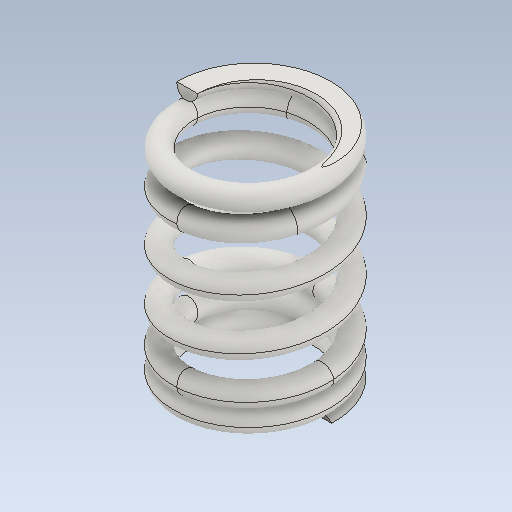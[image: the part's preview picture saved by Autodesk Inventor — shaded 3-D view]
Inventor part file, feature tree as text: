
AUTODESK INVENTOR PART (.ipt)
format: ipt  version: 2021 (Build 250183000, 183)  size: 877,568 bytes
history: native  units: in
note: dims shown in document units (in); Inventor stores cm internally (conversion verified against a paired STEP export)
features: other x73, extrude x8, sweep x2, helix x2, plane x1
ambient origin geometry x8: Origin, YZ Plane, XZ Plane, XY Plane, X Axis, Y Axis, Z Axis, Center Point
bodies: Solid1 (feature_tree)
feature tree (86):
  other  "Main Coil Path(Right)"
  other  "Section Work Plane(Right)"
  other  "Start Work Plane(Right)"
  other  "End Work Plane(Right)"
  other  "End Cut Work Plane(Right)"
  other  "Start Cut Work Plane(Right)"
  other  "Plain Ends Cut Work Plane 1(Right)"
  other  "Plain Ends Cut Work Plane 2(Right)"
  sweep  "Main Coil Feature(R)"
  other  "Start Transition Coil 1(Right)"
  other  "Start Transition Coil 2(Right)"
  other  "Start Transition Coil 3(Right)"
  other  "Start Transition Coil 4(Right)"
  other  "Start Ends Coil(Right)"
  extrude  "Start Cut Feature(Right)"  Depth=0.4866in
  other  "End Transition Coil 1(Right)"
  other  "End Transition Coil 2(Right)"
  other  "End Transition Coil 3(Right)"
  other  "End Transition Coil 4(Right)"
  other  "End Coil(Right)"
  extrude  "End Cut Feature(Right)"  Depth=0.4306in
  extrude  "Plain Ends Cut Feature 1(Right)"  Depth=0.2in
  extrude  "Plain Ends Cut Feature 2(Right)"  TaperAngle=0.0deg  [1 undecoded]
  other  "Main Coil Path(Left)"
  other  "Section Work Plane(Left)"
  other  "Start Work Plane(Left)"
  other  "End Work Plane(Left)"
  other  "End Cut Work Plane(Left)"
  other  "Start Cut Work Plane(Left)"
  other  "Plain Ends Cut Work Plane 1(Left)"
  other  "Plain Ends Cut Work Plane 2(Left)"
  sweep  "Main Coil Feature(L)"
  other  "Start Transition Coil 1(Left)"
  other  "Start Transition Coil 2(Left)"
  other  "Start Transition Coil 3(Left)"
  other  "Start Transition Coil 4(Left)"
  other  "Start Ends Coil(Left)"
  extrude  "Start Cut Feature(Left)"  Depth=0.2014in
  other  "End Transition Coil 1(Left)"
  other  "End Transition Coil 2(Left)"
  other  "End Transition Coil 3(Left)"
  other  "End Transition Coil 4(Left)"
  other  "End Coil(Left)"
  extrude  "End Cut Feature(Left)"  Depth=0.3937in
  extrude  "Cut Plain Ends Cut 1(L)"  Depth=1.5in
  extrude  "Cut Plain Ends Cut 2(L)"  Depth=0.2in
  other  "iMate Based Work Plane"
  other  "Preview Center Point"
  other  "Preview X Axis"
  other  "Path Section Sketch(Right)"
  other  "Srf1"
  helix  "Coil Section Sketch(Right)"  [1 undecoded]
  other  "Start Transition Coil Sketch 1(Right)"
  other  "Start Transition Coil Sketch 2(Right)"
  other  "Start Transition Coil Sketch 3(Right)"
  other  "Start Transition Coil Sketch 4(Right)"
  other  "End Transition Coil Sketch 1(Right)"
  other  "End Transition Coil Sketch 2(Right)"
  other  "End Transition Coil Sketch 3(Right)"
  other  "End Transition Coil Sketch 4(Right)"
  other  "Start Ends Skecth(Right)"
  other  "End Coil Skecth(Right)"
  other  "Start Cut Sketch(Right)"
  other  "End Cut Sketch(Right)"
  other  "Plain Ends Cut Sketch 2(Right)"
  other  "Plain Ends Cut Sketch 1(Right)"
  other  "Path Section Sketch(Left)"
  other  "Srf2"
  helix  "Coil Section Sketch(Left)"  [1 undecoded]
  other  "Start Transition Coil Sketch 1(Left)"
  other  "Start Transition Coil Sketch 2(Left)"
  other  "Start Transition Coil Sketch 3(Left)"
  other  "Start Transition Coil Sketch 4(Left)"
  other  "Start Ends Skecth(Left)"
  other  "Start Cut Sketch(Left)"
  other  "End Transition Coil Sketch 1(Left)"
  other  "End Transition Coil Sketch 2(Left)"
  other  "End Transition Coil Sketch 3(Left)"
  other  "End Transition Coil Sketch 4(Left)"
  other  "End Coil Skecth(Left)"
  other  "End Cut Sketch(Left)"
  other  "Plain Ends Cut Sketch 2(Left)"
  other  "Plain Ends Cut Sketch 1(Left)"
  plane  "Work Plane Start Section"
  other  "Basic Curve(Right)"
  other  "Basic Curve(Left)"
note: 3 required parameter values undecoded (feature->parameter linkage not recoverable at this tier; creation-order binding heuristic only, values carry confidence <= 0.55)
